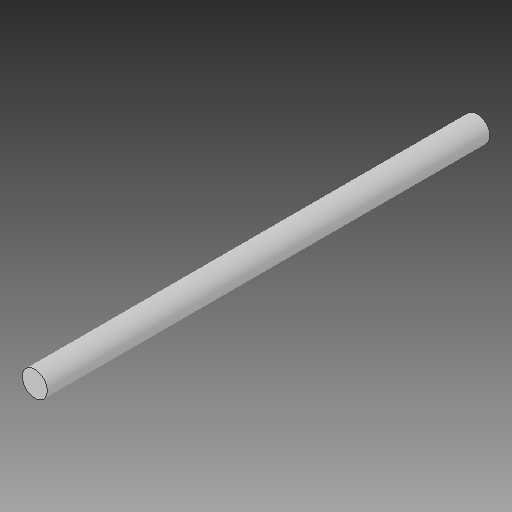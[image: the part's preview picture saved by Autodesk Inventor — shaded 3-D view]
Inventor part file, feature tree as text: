
AUTODESK INVENTOR PART (.ipt)
format: ipt  version: 2019 (Build 230136000, 136)  size: 77,312 bytes
history: native  units: in
note: dims shown in document units (in); Inventor stores cm internally (conversion verified against a paired STEP export)
features: other x3, sketch x1
ambient origin geometry x8: Origin, YZ Plane, XZ Plane, XY Plane, X Axis, Y Axis, Z Axis, Center Point
bodies: Solid1 (feature_tree)
feature tree (4):
  other  "4inax.ipt"
  other  "Solid1::4inax.ipt"
  other  "TaggingFeature1"
  sketch  "Sketch1"  dims[d0=0.3937in]
